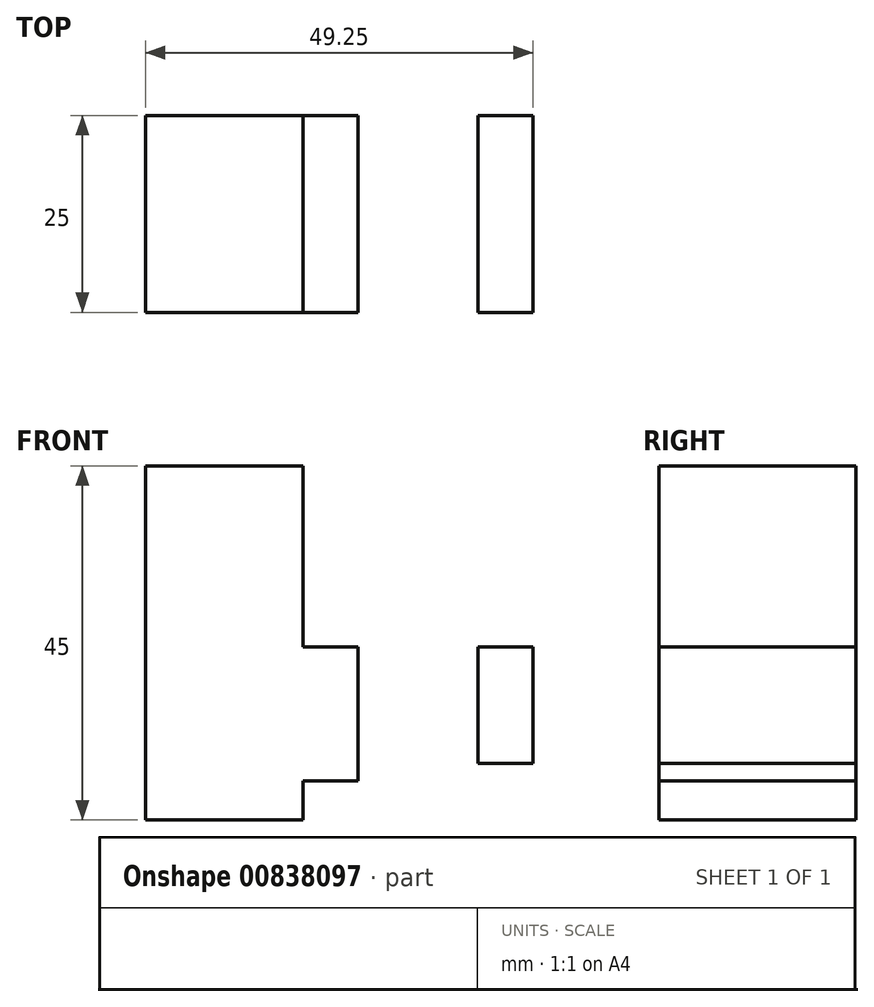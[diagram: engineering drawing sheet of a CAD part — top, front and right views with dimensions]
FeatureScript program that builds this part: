
annotation { "Feature Type Name" : "Feature", "Feature Type Description" : "" }
export const myFeature = defineFeature(function(context is Context, id is Id, definition is map)
    precondition{}
    {
        {
            var Q0;
            Q0=qCreatedBy(makeId("Front.planeOp"),FACE);
            var sketch = newSketch(context, id + "F0", { "sketchPlane" : qUnion([Q0])});
            skLineSegment(sketch, "E0.top", {"start": v(-10, -17.5) * mm, "end": v(10, -17.5) * mm});
            skLineSegment(sketch, "E0.left", {"start": v(-10, 17.5) * mm, "end": v(-10, -17.5) * mm});
            skLineSegment(sketch, "E0.right", {"start": v(10, 17.5) * mm, "end": v(10, -17.5) * mm});
            skPoint(sketch, "E0.middle", {"position": v(0, 0) * mm});
            skLineSegment(sketch, "E1.bottom", {"start": v(-10, 17.5) * mm, "end": v(10, 17.5) * mm, "construction": true});
            skLineSegment(sketch, "E1.top", {"start": v(-10, 27.5) * mm, "end": v(10, 27.5) * mm});
            skLineSegment(sketch, "E1.left", {"start": v(-10, 17.5) * mm, "end": v(-10, 27.5) * mm});
            skLineSegment(sketch, "E1.right", {"start": v(10, 17.5) * mm, "end": v(10, 27.5) * mm});
            skLineSegment(sketch, "E2.left", {"start": v(10, -17.5) * mm, "end": v(10, -12.5) * mm});
            skLineSegment(sketch, "E3.top", {"start": v(10, 4.5) * mm, "end": v(17, 4.5) * mm});
            skLineSegment(sketch, "E3.left", {"start": v(10, -12.5) * mm, "end": v(10, 4.5) * mm});
            skLineSegment(sketch, "E4", {"start": v(10, -12.5) * mm, "end": v(17, -12.5) * mm});
            skLineSegment(sketch, "E5.bottom", {"start": v(32.25, 4.5) * mm, "end": v(39.25, 4.5) * mm});
            skLineSegment(sketch, "E5.top", {"start": v(32.25, -10.3) * mm, "end": v(39.25, -10.3) * mm});
            skLineSegment(sketch, "E5.left", {"start": v(32.25, 4.5) * mm, "end": v(32.25, -10.3) * mm});
            skLineSegment(sketch, "E5.right", {"start": v(39.25, 4.5) * mm, "end": v(39.25, -10.3) * mm});
            skLineSegment(sketch, "E6", {"start": v(17, 4.5) * mm, "end": v(17, -12.5) * mm});
            skSolve(sketch);
        }
        {
            var Q0;
            Q0 = qSketchRegion(id + "F0", true);
            extrude(context, id + "F1", {"entities" : qUnion([Q0]), "depth" : 25 * mm, "offsetDistance" : 25 * mm});
        }
    });
